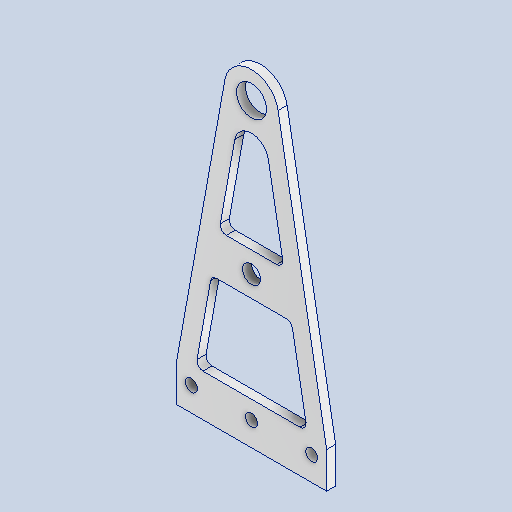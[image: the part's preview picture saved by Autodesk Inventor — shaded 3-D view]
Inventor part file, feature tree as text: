
AUTODESK INVENTOR PART (.ipt)
format: ipt  version: 2025.1 (Build 291241000, 241)  size: 312,832 bytes
history: native  units: mm
features: sketch x6, extrude x3, hole x3, fillet x1
ambient origin geometry x8: Origin, YZ Plane, XZ Plane, XY Plane, X Axis, Y Axis, Z Axis, Center Point
bodies: Volumenkörper1 (feature_tree)
feature tree (13):
  extrude  "Extrusion1"  Depth=100.0mm
  hole  "Bohrung1"  [1 undecoded]
  extrude  "Extrusion2"  Depth=2.0mm
  extrude  "Extrusion3"  Depth=43.0mm
  hole  "Bohrung2"  [1 undecoded]
  fillet  "Rundung1"  Radius=14.0mm
  hole  "Bohrung3"  [1 undecoded]
  sketch  "Skizze1"  dims[d0=100.0mm d1=12.0mm]
  sketch  "Skizze3"  dims[d2=50.0mm d3=9.0mm]
  sketch  "Skizze4"  dims[d4=3.0mm d5=0.0mm]
  sketch  "Skizze5"  dims[d6=10.0mm d7=6.0mm d8=4.0mm d9=2.0mm d10=90.0deg d11=8.0mm d12=0.0mm d13=15.0mm]
  sketch  "Skizze6"  dims[d14=6.0mm d15=43.0mm]
  sketch  "Skizze7"  dims[d16=3.0mm d17=0.0mm d18=6.0mm d19=14.0mm d20=14.0mm d21=10.0mm d22=0.0mm d23=6.0mm d24=6.0mm d25=4.0mm d26=2.0mm d27=90.0deg d28=8.0mm d29=0.0mm d30=7.0mm d31=2.0mm d32=4.0mm d33=6.0mm d34=4.0mm d35=2.0mm d36=90.0deg d37=8.0mm d38=0.0mm d39=5.0mm d40=5.0mm d41=20.0mm d42=8.0mm]
note: 3 required parameter values undecoded (feature->parameter linkage not recoverable at this tier; creation-order binding heuristic only, values carry confidence <= 0.55)
